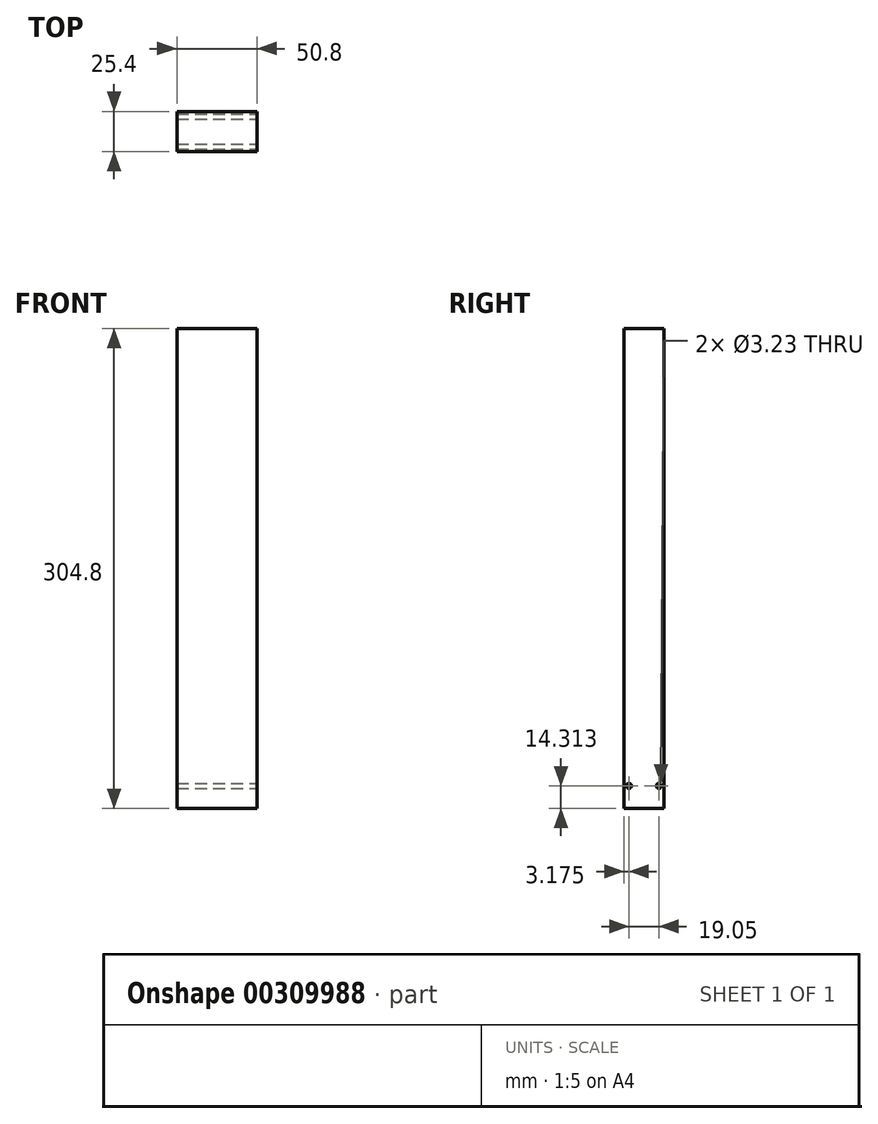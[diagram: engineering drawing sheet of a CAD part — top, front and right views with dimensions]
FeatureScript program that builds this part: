
annotation { "Feature Type Name" : "Feature", "Feature Type Description" : "" }
export const myFeature = defineFeature(function(context is Context, id is Id, definition is map)
    precondition{}
    {
        {
            var Q0;
            Q0=qCreatedBy(makeId("Top.planeOp"),FACE);
            var sketch = newSketch(context, id + "F0", { "sketchPlane" : qUnion([Q0])});
            skLineSegment(sketch, "E0.bottom", {"start": v(-25.4, 12.7) * mm, "end": v(25.4, 12.7) * mm});
            skLineSegment(sketch, "E0.top", {"start": v(-25.4, -12.7) * mm, "end": v(25.4, -12.7) * mm});
            skLineSegment(sketch, "E0.left", {"start": v(-25.4, 12.7) * mm, "end": v(-25.4, -12.7) * mm});
            skLineSegment(sketch, "E0.right", {"start": v(25.4, 12.7) * mm, "end": v(25.4, -12.7) * mm});
            skPoint(sketch, "E0.middle", {"position": v(0, 0) * mm});
            skSolve(sketch);
        }
        {
            var Q0;
            Q0=makeQuery(id+"F0.imprint","IMPRINT",FACE,{"disambiguationData":[TD([[makeQuery(id+"F0.imprint","IMPRINT",EDGE,{"derivedFrom":sQuery(id+"F0.wireOp",EDGE,"E0.bottom")}),-1.0]])]});
            extrude(context, id + "F1", {"entities" : qUnion([Q0]), "depth" : 304.8 * mm});
        }
        {
            var Q0;
            Q0=makeQuery(id+"F1.opExtrude","SWEPT_FACE",FACE,{"disambiguationData":[OSD([sQuery(id+"F0.wireOp",EDGE,"E0.right")])]});
            var sketch = newSketch(context, id + "F2", { "sketchPlane" : qUnion([Q0])});
            skCircle(sketch, "E1", {"center": v(-9.52, 14.31) * mm, "radius": 1.61 * mm});
            skCircle(sketch, "E2.1.0.0", {"center": v(9.53, 14.31) * mm, "radius": 1.61 * mm});
            skLineSegment(sketch, "E2.direction1", {"start": v(-9.52, 14.31) * mm, "end": v(9.53, 14.31) * mm, "construction": true});
            skSolve(sketch);
        }
        {
            var Q0;
            Q0=sQuery(id+"F2.wireOp",VERTEX,"E2.1.0.0.center");
            var Q1;
            Q1=sQuery(id+"F2.wireOp",VERTEX,"E1.center");
            var Q2;
            Q2=makeQuery(id+"F1.opExtrude","SWEPT_BODY",BODY,{"disambiguationData":[OSD([sQuery(id+"F0.wireOp",EDGE,"E0.bottom"),sQuery(id+"F0.wireOp",EDGE,"E0.top"),sQuery(id+"F0.wireOp",EDGE,"E0.left"),sQuery(id+"F0.wireOp",EDGE,"E0.right")])]});
            hole(context, id + "F3", {"style" : HoleStyle.SIMPLE, "endStyle" : HoleEndStyle.THROUGH, "holeDiameter" : 3.23 * mm, "tappedDepth" : 12.7 * mm, "tapClearance" : 3, "locations" : qUnion([Q0, Q1]), "scope" : qUnion([Q2])});
        }
    });
